# Revit family: DH 8P CRUCETA ALUVIA
name_source: partatom
category: Aparatos sanitarios
revit_build: Autodesk Revit 2018 (Build: 20170223_1515(x64)
units: mm (PartAtom-declared; Revit-internal decimal feet)

## family parameters
Anfitrión = Muro
Compartido = No
Corte con vacíos al cargar = No
Cota de conector redondo = Diámetro de uso
Número OmniClass = 23.45.55.17
Punto de cálculo de habitación = No
Siempre vertical = Sí
Tipo de pieza = Normal
Título OmniClass = Mixing Faucets

## types (1)
- Tipo 1
    Acabado = Brillante
    Altura Nominal = 360
    Ancho Nominal = 118
    Características = Ultra ahorro de agua, cierre fácil giro de 90ª, funciones de chorro tipo lluvia e hidromasaje, tecnología anti-taponamiento, evita acumulación de impiurezas, fácil limpieza, brazo largo que permite bañarse a una mayor distancia
    Caudal = Promedio modo lluvia 5,8l/min. 80 psi, promedio modo hidromasaje 6,22l/min. 8' psi
    Color = Cromo
    Consumo de agua = 7,3l/min
    Cumplimiento de Norma = Ahorro de agua (7,3l/min.) cumple norma NTC 1644
    Código de montaje = D2010710
    Descripción = Showers
    Descripción IFC = Aluvia Grifería ducha 8 pulgadas triceta
    Descripción de la garantía = Garantía de 30 años por defectos de fabricación, garantía de 3 años en acabados.
    Diámetro de conexión entrada = 1/2 Pulg.
    Duración Garantía Partes = 30
    Duración Garantía Unidad = Años
    Fabricante = www.corona.com.co
    Forma = Cilindríca
    Información del producto = https://corona.co
    Logitud Nominal = 363
    Material = Cromo-Corona
    Material Secundario = Latón, recubrimiento cromo (acabados)
    Nombre = Ducha Aluvia
    Nombre del Fabricante = Corona
    Número Modelo = AV4020001
    Presión Máxima = 125 psi
    Presión mínima = 20 psi.
    Requerimientos Accesibilidad = Manual
    Responsable Garantías Partes = www.corona.com.co
    Tamaño = 363 x 118 x 360
    Tipo de Activo = Fijo
    Tráfico = Residencial
    Vida útil = 250000
    Vida útil unidad = Ciclos
